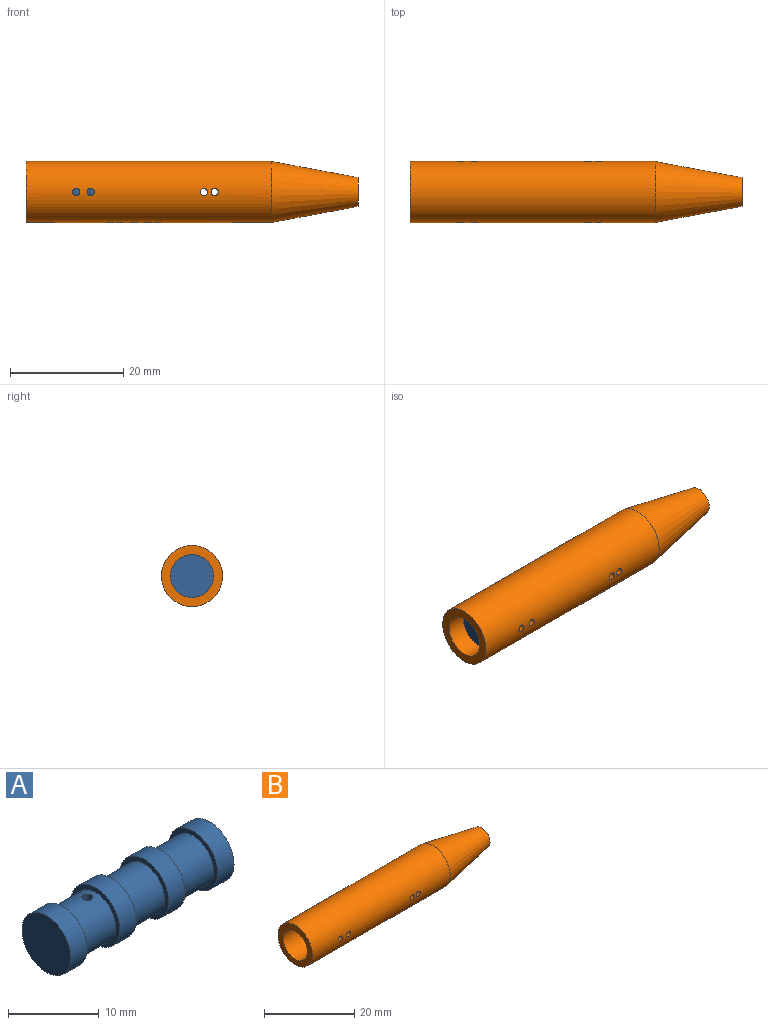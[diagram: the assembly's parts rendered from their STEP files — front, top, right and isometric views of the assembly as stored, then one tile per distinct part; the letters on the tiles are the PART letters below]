
ASSEMBLY  parts=2 mates=1
PART A: 19 faces, bbox 25.4x7.6x7.6 mm
  f0: cylinder r=3.17mm len=6.35mm, axis (-1,0,0), area 100.2mm2, adj f11,f12,f18
  f1: cylinder r=3.17mm len=6.35mm, axis (-1,0,0), area 100.2mm2, adj f4,f5,f16
  f2: plane 7.62x7.62mm, normal (1,0,0), area 45.6mm2, adj f3
  f3: cylinder r=3.81mm len=7.62mm, axis (-1,0,0), area 60.8mm2, adj f2,f4
  f4: plane 7.62x7.62mm, normal (-1,0,0), area 13.9mm2, adj f1,f3
  f5: plane 7.62x7.62mm, normal (1,0,0), area 13.9mm2, adj f1,f6
  f6: cylinder r=3.81mm len=7.62mm, axis (-1,0,0), area 60.8mm2, adj f5,f7
  f7: plane 7.62x7.62mm, normal (-1,0,0), area 13.9mm2, adj f6,f8
  f8: cylinder r=3.17mm len=6.35mm, axis (-1,0,0), area 101.3mm2, adj f7,f9
  f9: plane 7.62x7.62mm, normal (1,0,0), area 13.9mm2, adj f8,f10
  f10: cylinder r=3.81mm len=7.62mm, axis (-1,0,0), area 60.8mm2, adj f9,f11
  f11: plane 7.62x7.62mm, normal (-1,0,0), area 13.9mm2, adj f0,f10
  f12: plane 7.62x7.62mm, normal (1,0,0), area 13.9mm2, adj f0,f13
  f13: cylinder r=3.81mm len=7.62mm, axis (-1,0,0), area 60.8mm2, adj f12,f14
  f14: plane 7.62x7.62mm, normal (-1,0,0), area 45.6mm2, adj f13
  f15: plane 1.19x1.19mm, normal (0,0,-1), area 1.1mm2, adj f16
  f16: cylinder r=0.6mm len=3.18mm, axis (0,0,1), area 11.8mm2, adj f1,f15
  f17: plane 1.19x1.19mm, normal (0,0,1), area 1.1mm2, adj f18
  f18: cylinder r=0.6mm len=3.18mm, axis (0,0,-1), area 11.8mm2, adj f0,f17
PART B: 21 faces, bbox 58.7x10.8x10.8 mm
  f0: plane 7.62x7.62mm, normal (-1,0,0), area 45.6mm2, adj f7
  f1: plane 2.5x2.5mm, normal (1,0,0), area 4.9mm2, adj f2
  f2: cylinder r=1.25mm len=12.41mm, axis (-1,0,0), area 97.3mm2, adj f1,f3
  f3: plane 5.09x5.09mm, normal (1,0,0), area 15.5mm2, adj f2,f4
  f4: cone r=2.55mm half-angle=10.5deg, axis (-1,0,0), area 389.9mm2, adj f3,f5
  f5: cylinder r=5.4mm len=43.32mm, axis (-1,0,0), area 1452.6mm2, adj f4,f6,f8,f9,f10,f11,f12,f13
  f6: plane 10.8x10.8mm, normal (-1,0,0), area 45.9mm2, adj f5,f7
  f7: cylinder r=3.81mm len=38.1mm, axis (-1,0,0), area 895.6mm2, adj f0,f6,f8,f9,f10,f11,f12,f13
  f8: cylinder r=0.64mm len=1.64mm, axis (0,0,1), area 6.4mm2, adj f5,f7
  f9: cylinder r=0.64mm len=1.64mm, axis (0,0,1), area 6.4mm2, adj f5,f7
  f10: cylinder r=0.64mm len=1.64mm, axis (0,0,1), area 6.4mm2, adj f5,f7
  f11: cylinder r=0.64mm len=1.64mm, axis (0,0,1), area 6.4mm2, adj f5,f7
  f12: cylinder r=0.64mm len=1.64mm, axis (0,0,1), area 6.4mm2, adj f5,f7
  f13: cylinder r=0.64mm len=1.64mm, axis (0,-1,0), area 6.4mm2, adj f5,f7
  f14: cylinder r=0.64mm len=1.64mm, axis (0,-1,0), area 6.4mm2, adj f5,f7
  f15: cylinder r=0.64mm len=1.64mm, axis (0,-1,0), area 6.4mm2, adj f5,f7
  f16: cylinder r=0.64mm len=1.64mm, axis (0,-1,0), area 6.4mm2, adj f5,f7
  f17: cylinder r=0.64mm len=1.64mm, axis (0,-1,0), area 6.4mm2, adj f5,f7
  f18: cylinder r=0.64mm len=1.64mm, axis (0,-1,0), area 6.4mm2, adj f5,f7
  f19: cylinder r=0.64mm len=1.64mm, axis (0,-1,0), area 6.4mm2, adj f5,f7
  f20: cylinder r=0.64mm len=1.64mm, axis (0,-1,0), area 6.4mm2, adj f5,f7
PLACE A rot(axis=(1,0,0),176.4deg) t=(3.63,0,0)mm
PLACE B at identity fixed
MATE cylindrical B.f2 <-> A.f0  axis (-1,0,0) through (0,0,0)mm
